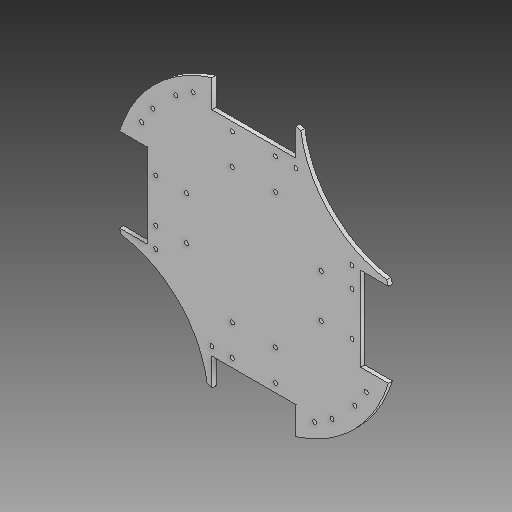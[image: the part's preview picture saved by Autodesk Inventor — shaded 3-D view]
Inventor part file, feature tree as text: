
AUTODESK INVENTOR PART (.ipt)
format: ipt  version: 2020 (Build 240168000, 168)  size: 204,800 bytes
history: native  units: mm
features: extrude x2, sketch x2, other x1
ambient origin geometry x8: Origin, YZ Plane, XZ Plane, XY Plane, X Axis, Y Axis, Z Axis, Center Point
bodies: Body1 (feature_tree)
feature tree (5):
  other  "Твердое тело1"
  extrude  "Выдавливание1"  Depth=215.0mm
  extrude  "Выдавливание2"  Depth=208.0mm
  sketch  "Эскиз2"
  sketch  "Эскиз3"
